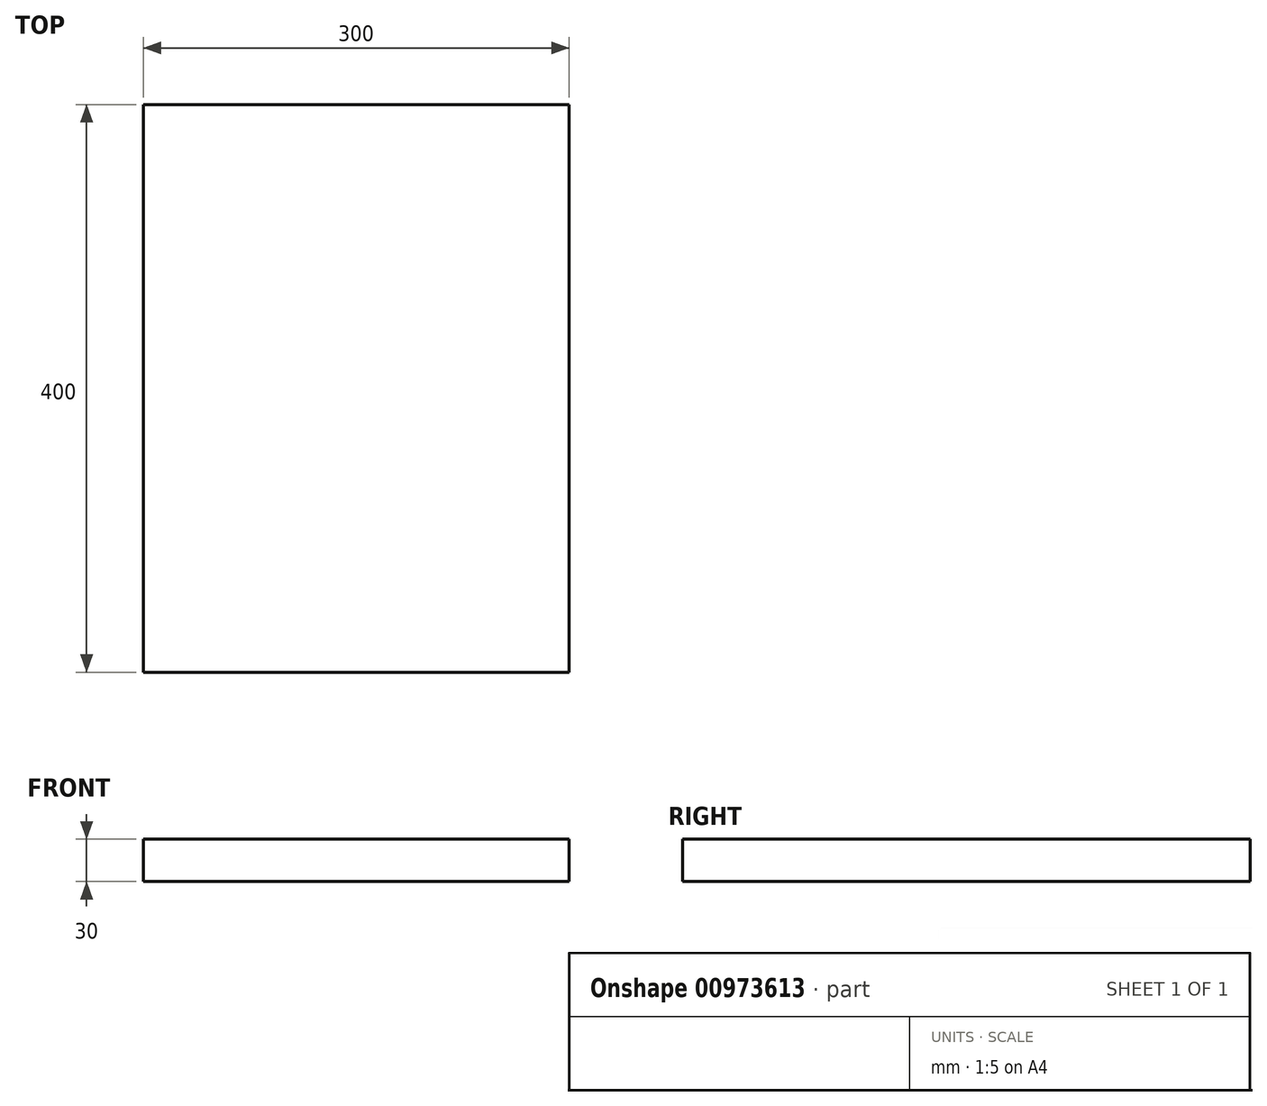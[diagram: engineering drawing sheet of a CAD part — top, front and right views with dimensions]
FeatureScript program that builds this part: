
annotation { "Feature Type Name" : "Feature", "Feature Type Description" : "" }
export const myFeature = defineFeature(function(context is Context, id is Id, definition is map)
    precondition{}
    {
        {
            var Q0;
            Q0=qCreatedBy(makeId("Top.planeOp"),FACE);
            var sketch = newSketch(context, id + "F0", { "sketchPlane" : qUnion([Q0])});
            skLineSegment(sketch, "E0.bottom", {"start": v(150, 200) * mm, "end": v(-150, 200) * mm});
            skLineSegment(sketch, "E0.top", {"start": v(150, -200) * mm, "end": v(-150, -200) * mm});
            skLineSegment(sketch, "E0.left", {"start": v(150, 200) * mm, "end": v(150, -200) * mm});
            skLineSegment(sketch, "E0.right", {"start": v(-150, 200) * mm, "end": v(-150, -200) * mm});
            skPoint(sketch, "E0.middle", {"position": v(0, 0) * mm});
            skSolve(sketch);
        }
        {
            var Q0;
            Q0=makeQuery(id+"F0.imprint","IMPRINT",FACE,{"disambiguationData":[TD([[makeQuery(id+"F0.imprint","IMPRINT",EDGE,{"derivedFrom":sQuery(id+"F0.wireOp",EDGE,"E0.bottom")}),1.0]])]});
            extrude(context, id + "F1", {"entities" : qUnion([Q0]), "depth" : 30 * mm, "offsetDistance" : 25 * mm});
        }
    });
